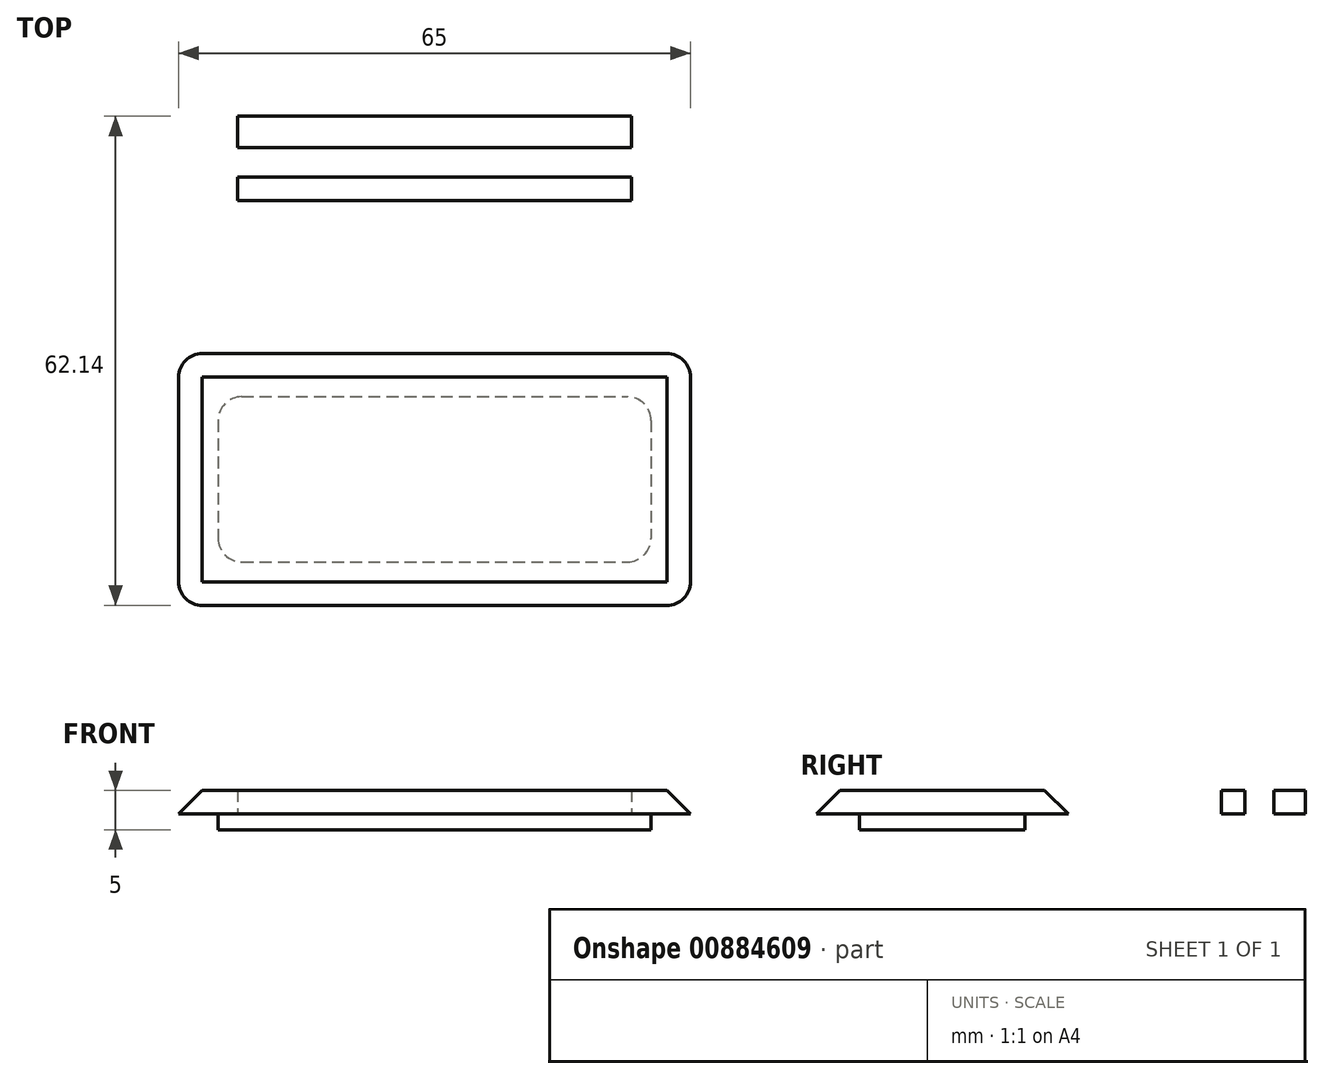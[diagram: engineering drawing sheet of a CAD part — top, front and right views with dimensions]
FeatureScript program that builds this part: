
annotation { "Feature Type Name" : "Feature", "Feature Type Description" : "" }
export const myFeature = defineFeature(function(context is Context, id is Id, definition is map)
    precondition{}
    {
        {
            var Q0;
            Q0=qCreatedBy(makeId("Top.planeOp"),FACE);
            var sketch = newSketch(context, id + "F0", { "sketchPlane" : qUnion([Q0])});
            skLineSegment(sketch, "E0.bottom", {"start": v(-29.5, 16) * mm, "end": v(29.5, 16) * mm});
            skLineSegment(sketch, "E0.top", {"start": v(-29.5, -16) * mm, "end": v(29.5, -16) * mm});
            skLineSegment(sketch, "E0.left", {"start": v(-32.5, 13) * mm, "end": v(-32.5, -13) * mm});
            skLineSegment(sketch, "E0.right", {"start": v(32.5, 13) * mm, "end": v(32.5, -13) * mm});
            skPoint(sketch, "E0.middle", {"position": v(0, 0) * mm});
            skLineSegment(sketch, "E1.bottom", {"start": v(-24.5, 10.5) * mm, "end": v(24.5, 10.5) * mm});
            skLineSegment(sketch, "E1.top", {"start": v(-24.5, -10.5) * mm, "end": v(24.5, -10.5) * mm});
            skLineSegment(sketch, "E1.left", {"start": v(-27.5, 7.5) * mm, "end": v(-27.5, -7.5) * mm});
            skLineSegment(sketch, "E1.right", {"start": v(27.5, 7.5) * mm, "end": v(27.5, -7.5) * mm});
            skPoint(sketch, "E2.visualSharp", {"position": v(-27.5, 10.5) * mm});
            skArc(sketch, "E2.filletArc", {"start": v(-24.5, 10.5) * mm, "mid": v(-26.62, 9.62) * mm, "end": v(-27.5, 7.5) * mm});
            skPoint(sketch, "E3.visualSharp", {"position": v(-27.5, -10.5) * mm});
            skArc(sketch, "E3.filletArc", {"start": v(-27.5, -7.5) * mm, "mid": v(-26.62, -9.62) * mm, "end": v(-24.5, -10.5) * mm});
            skPoint(sketch, "E4.visualSharp", {"position": v(27.5, -10.5) * mm});
            skArc(sketch, "E4.filletArc", {"start": v(24.5, -10.5) * mm, "mid": v(26.62, -9.62) * mm, "end": v(27.5, -7.5) * mm});
            skPoint(sketch, "E5.visualSharp", {"position": v(27.5, 10.5) * mm});
            skArc(sketch, "E5.filletArc", {"start": v(27.5, 7.5) * mm, "mid": v(26.62, 9.62) * mm, "end": v(24.5, 10.5) * mm});
            skPoint(sketch, "E6.visualSharp", {"position": v(-32.5, 16) * mm});
            skArc(sketch, "E6.filletArc", {"start": v(-29.5, 16) * mm, "mid": v(-31.62, 15.12) * mm, "end": v(-32.5, 13) * mm});
            skPoint(sketch, "E7.visualSharp", {"position": v(-32.5, -16) * mm});
            skArc(sketch, "E7.filletArc", {"start": v(-32.5, -13) * mm, "mid": v(-31.62, -15.12) * mm, "end": v(-29.5, -16) * mm});
            skPoint(sketch, "E8.visualSharp", {"position": v(32.5, -16) * mm});
            skArc(sketch, "E8.filletArc", {"start": v(29.5, -16) * mm, "mid": v(31.62, -15.12) * mm, "end": v(32.5, -13) * mm});
            skPoint(sketch, "E9.visualSharp", {"position": v(32.5, 16) * mm});
            skArc(sketch, "E9.filletArc", {"start": v(32.5, 13) * mm, "mid": v(31.62, 15.12) * mm, "end": v(29.5, 16) * mm});
            skSolve(sketch);
        }
        {
            var Q0;
            Q0=makeQuery(id+"F0.imprint","IMPRINT",FACE,{"disambiguationData":[TD([[makeQuery(id+"F0.imprint","IMPRINT",EDGE,{"derivedFrom":sQuery(id+"F0.wireOp",EDGE,"E0.bottom")}),-1.0]])]});
            var Q1;
            Q1=makeQuery(id+"F0.imprint","IMPRINT",FACE,{"disambiguationData":[TD([[makeQuery(id+"F0.imprint","IMPRINT",EDGE,{"derivedFrom":sQuery(id+"F0.wireOp",EDGE,"E1.bottom")}),-1.0]])]});
            extrude(context, id + "F1", {"entities" : qUnion([Q0, Q1]), "depth" : 3 * mm, "offsetDistance" : 25 * mm, "hasDraft" : true, "draftAngle" : 45 * degree, "draftPullDirection" : true});
        }
        {
            var Q0;
            Q0=makeQuery(id+"F0.imprint","IMPRINT",FACE,{"disambiguationData":[TD([[makeQuery(id+"F0.imprint","IMPRINT",EDGE,{"derivedFrom":sQuery(id+"F0.wireOp",EDGE,"E1.bottom")}),-1.0]])]});
            extrude(context, id + "F2", {"entities" : qUnion([Q0]), "operationType" : NewBodyOperationType.ADD, "oppositeDirection" : true, "depth" : 2 * mm, "offsetDistance" : 25 * mm});
        }
        {
            var Q0;
            Q0=qCreatedBy(makeId("Top.planeOp"),FACE);
            var sketch = newSketch(context, id + "F3", { "sketchPlane" : qUnion([Q0])});
            skLineSegment(sketch, "E10.bottom", {"start": v(-25, 46.14) * mm, "end": v(25, 46.14) * mm});
            skLineSegment(sketch, "E10.top", {"start": v(-25, 42.14) * mm, "end": v(25, 42.14) * mm});
            skLineSegment(sketch, "E10.left", {"start": v(-25, 46.14) * mm, "end": v(-25, 42.14) * mm});
            skLineSegment(sketch, "E10.right", {"start": v(25, 46.14) * mm, "end": v(25, 42.14) * mm});
            skLineSegment(sketch, "E11.bottom", {"start": v(-25, 35.44) * mm, "end": v(25, 35.44) * mm});
            skLineSegment(sketch, "E11.top", {"start": v(-25, 38.44) * mm, "end": v(25, 38.44) * mm});
            skLineSegment(sketch, "E11.left", {"start": v(-25, 35.44) * mm, "end": v(-25, 38.44) * mm});
            skLineSegment(sketch, "E11.right", {"start": v(25, 35.44) * mm, "end": v(25, 38.44) * mm});
            skSolve(sketch);
        }
        {
            var Q0;
            Q0=makeQuery(id+"F3.imprint","IMPRINT",FACE,{"disambiguationData":[TD([[makeQuery(id+"F3.imprint","IMPRINT",EDGE,{"derivedFrom":sQuery(id+"F3.wireOp",EDGE,"E11.bottom")}),1.0]])]});
            var Q1;
            Q1=makeQuery(id+"F3.imprint","IMPRINT",FACE,{"disambiguationData":[TD([[makeQuery(id+"F3.imprint","IMPRINT",EDGE,{"derivedFrom":sQuery(id+"F3.wireOp",EDGE,"E10.bottom")}),-1.0]])]});
            extrude(context, id + "F4", {"entities" : qUnion([Q0, Q1]), "depth" : 3 * mm, "offsetDistance" : 25 * mm});
        }
    });
